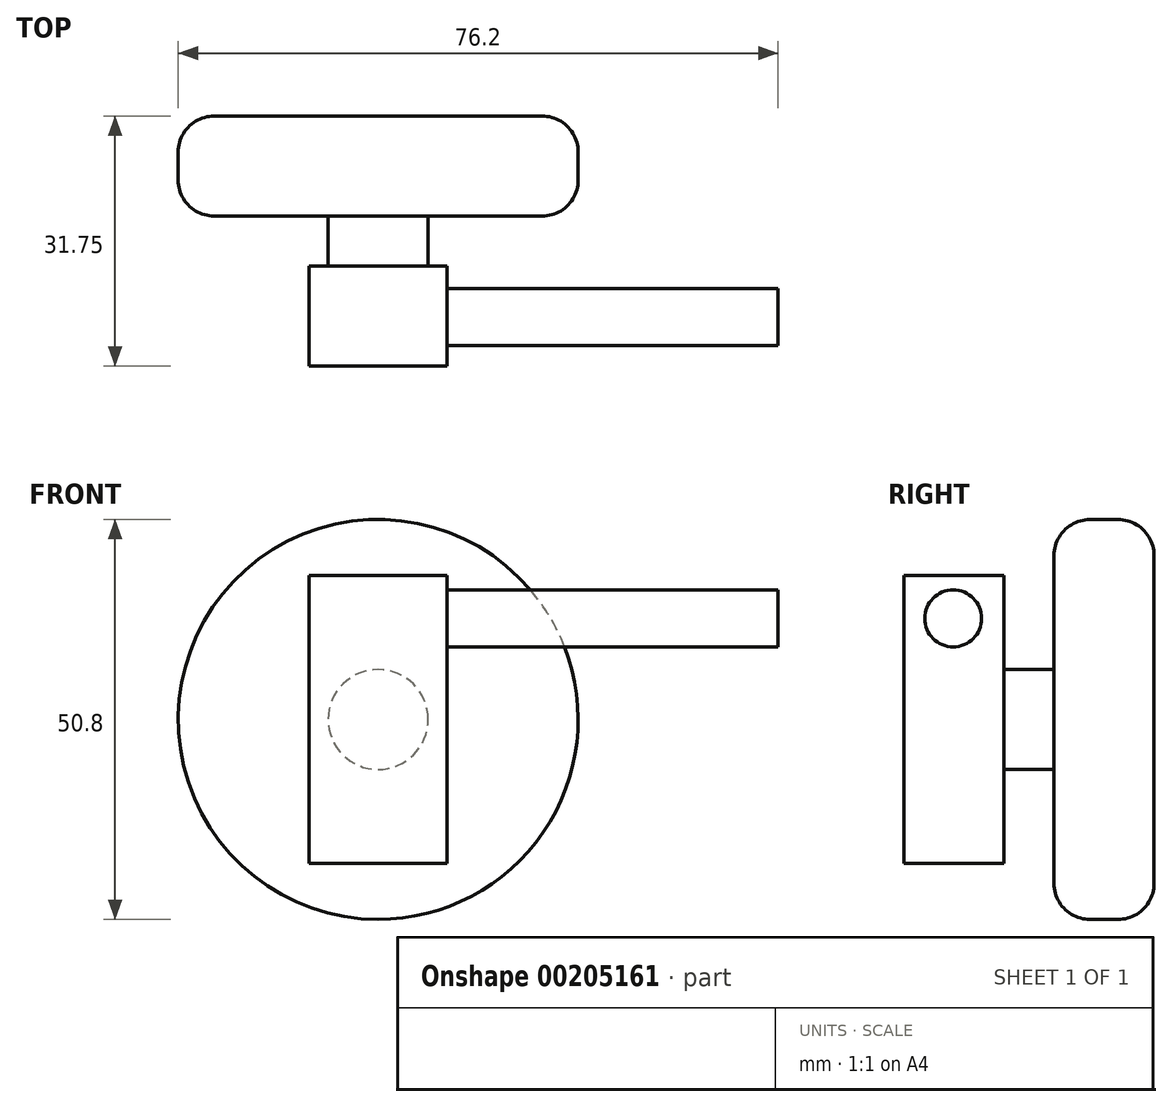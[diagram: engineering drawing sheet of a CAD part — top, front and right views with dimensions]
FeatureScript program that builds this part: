
annotation { "Feature Type Name" : "Feature", "Feature Type Description" : "" }
export const myFeature = defineFeature(function(context is Context, id is Id, definition is map)
    precondition{}
    {
        {
            var Q0;
            Q0=qCreatedBy(makeId("Front.planeOp"),FACE);
            var sketch = newSketch(context, id + "F0", { "sketchPlane" : qUnion([Q0])});
            skCircle(sketch, "E0", {"center": v(0, 0) * mm, "radius": 25.4 * mm});
            skSolve(sketch);
        }
        {
            var Q0;
            Q0=makeQuery(id+"F0.imprint","IMPRINT",FACE,{"disambiguationData":[TD([[makeQuery(id+"F0.imprint","IMPRINT",EDGE,{"derivedFrom":sQuery(id+"F0.wireOp",EDGE,"E0")}),1.0]])]});
            extrude(context, id + "F1", {"entities" : qUnion([Q0]), "depth" : 12.7 * mm});
        }
        {
            var Q0;
            Q0=makeQuery(id+"F1.opExtrude","CAP_EDGE",EDGE,{"disambiguationData":[OSD([sQuery(id+"F0.wireOp",EDGE,"E0")])],"isStart":false});
            var Q1;
            Q1=makeQuery(id+"F1.opExtrude","CAP_EDGE",EDGE,{"disambiguationData":[OSD([sQuery(id+"F0.wireOp",EDGE,"E0")])],"isStart":true});
            fillet(context, id + "F2", {"entities" : qUnion([Q0, Q1]), "radius" : 0 * yard, "tangentPropagation" : true, "allowEdgeOverflow" : false});
        }
        {
            var Q0;
            Q0=makeQuery(id+"F1.opExtrude","CAP_FACE",FACE,{"disambiguationData":[OSD([sQuery(id+"F0.wireOp",EDGE,"E0")])],"isStart":false});
            var sketch = newSketch(context, id + "F3", { "sketchPlane" : qUnion([Q0])});
            skCircle(sketch, "E1", {"center": v(0, 0) * mm, "radius": 6.35 * mm});
            skSolve(sketch);
        }
        {
            var Q0;
            Q0=makeQuery(id+"F3.imprint","IMPRINT",FACE,{"disambiguationData":[TD([[makeQuery(id+"F3.imprint","IMPRINT",EDGE,{"derivedFrom":sQuery(id+"F3.wireOp",EDGE,"E1")}),1.0]])]});
            extrude(context, id + "F4", {"entities" : qUnion([Q0]), "operationType" : NewBodyOperationType.ADD, "depth" : 12.7 * mm});
        }
        {
            var Q0;
            Q0=makeQuery(id+"F1.opExtrude","CAP_FACE",FACE,{"disambiguationData":[OSD([sQuery(id+"F0.wireOp",EDGE,"E0")])],"isStart":false});
            cPlane(context, id + "F5", {"entities" : qUnion([Q0]), "cplaneType" : CPlaneType.OFFSET, "offset" : 6.35 * mm, "width" : 0.17 * yard, "height" : 0.17 * yard});
        }
        {
            var Q0;
            Q0=qCreatedBy(id+"F5.planeOp",FACE);
            var sketch = newSketch(context, id + "F6", { "sketchPlane" : qUnion([Q0])});
            skLineSegment(sketch, "E2.bottom", {"start": v(8.75, -18.29) * mm, "end": v(-8.75, -18.29) * mm});
            skLineSegment(sketch, "E2.top", {"start": v(8.75, 18.29) * mm, "end": v(-8.75, 18.29) * mm});
            skLineSegment(sketch, "E2.left", {"start": v(8.75, -18.29) * mm, "end": v(8.75, 18.29) * mm});
            skLineSegment(sketch, "E2.right", {"start": v(-8.75, -18.29) * mm, "end": v(-8.75, 18.29) * mm});
            skPoint(sketch, "E2.middle", {"position": v(0, 0) * mm});
            skSolve(sketch);
        }
        {
            var Q0;
            Q0=makeQuery(id+"F6.imprint","IMPRINT",FACE,{"disambiguationData":[TD([[makeQuery(id+"F6.imprint","IMPRINT",EDGE,{"derivedFrom":sQuery(id+"F6.wireOp",EDGE,"E2.bottom")}),-1.0]])]});
            extrude(context, id + "F7", {"entities" : qUnion([Q0]), "operationType" : NewBodyOperationType.ADD, "depth" : 12.7 * mm});
        }
        {
            var Q0;
            Q0=qCreatedBy(makeId("Right.planeOp"),FACE);
            var sketch = newSketch(context, id + "F8", { "sketchPlane" : qUnion([Q0])});
            skCircle(sketch, "E3", {"center": v(-25.51, 12.84) * mm, "radius": 3.62 * mm});
            skSolve(sketch);
        }
        {
            var Q0;
            Q0 = qSketchRegion(id + "F8", true);
            extrude(context, id + "F9", {"entities" : qUnion([Q0]), "operationType" : NewBodyOperationType.ADD, "depth" : 50.8 * mm});
        }
    });
